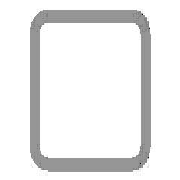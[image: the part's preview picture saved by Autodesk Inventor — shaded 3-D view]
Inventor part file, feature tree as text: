
AUTODESK INVENTOR PART (.ipt)
format: ipt  version: 2025 (Build 290162010, 162A)  size: 135,680 bytes
history: native  units: mm (DEFAULTED — no unit token found)
features: other x4, sketch x1, plane x1
ambient origin geometry x8: Origin, YZ Plane, XZ Plane, XY Plane, X Axis, Y Axis, Z Axis, Center Point
bodies: Solid1 (feature_tree), Body (feature_tree)
feature tree (6):
  parser-record x1  (decoder bookkeeping rows leaked as tree rows — omitted from the tree; the rows remain in map.json)
  other  "Driven Length"
  other  "Start Plane"
  other  "End Plane"
  sketch  "Sketch3"  dims[d3=1800.0mm d4=0.0mm d7=8.0mm d9=60.0mm d11=60.0mm d12=4.0mm d13=-0.0mm d14=1800.0mm d15=30.0mm d16=30.0mm d17=90.0deg d18=1800.0mm]
  plane  "Work Plane3"
